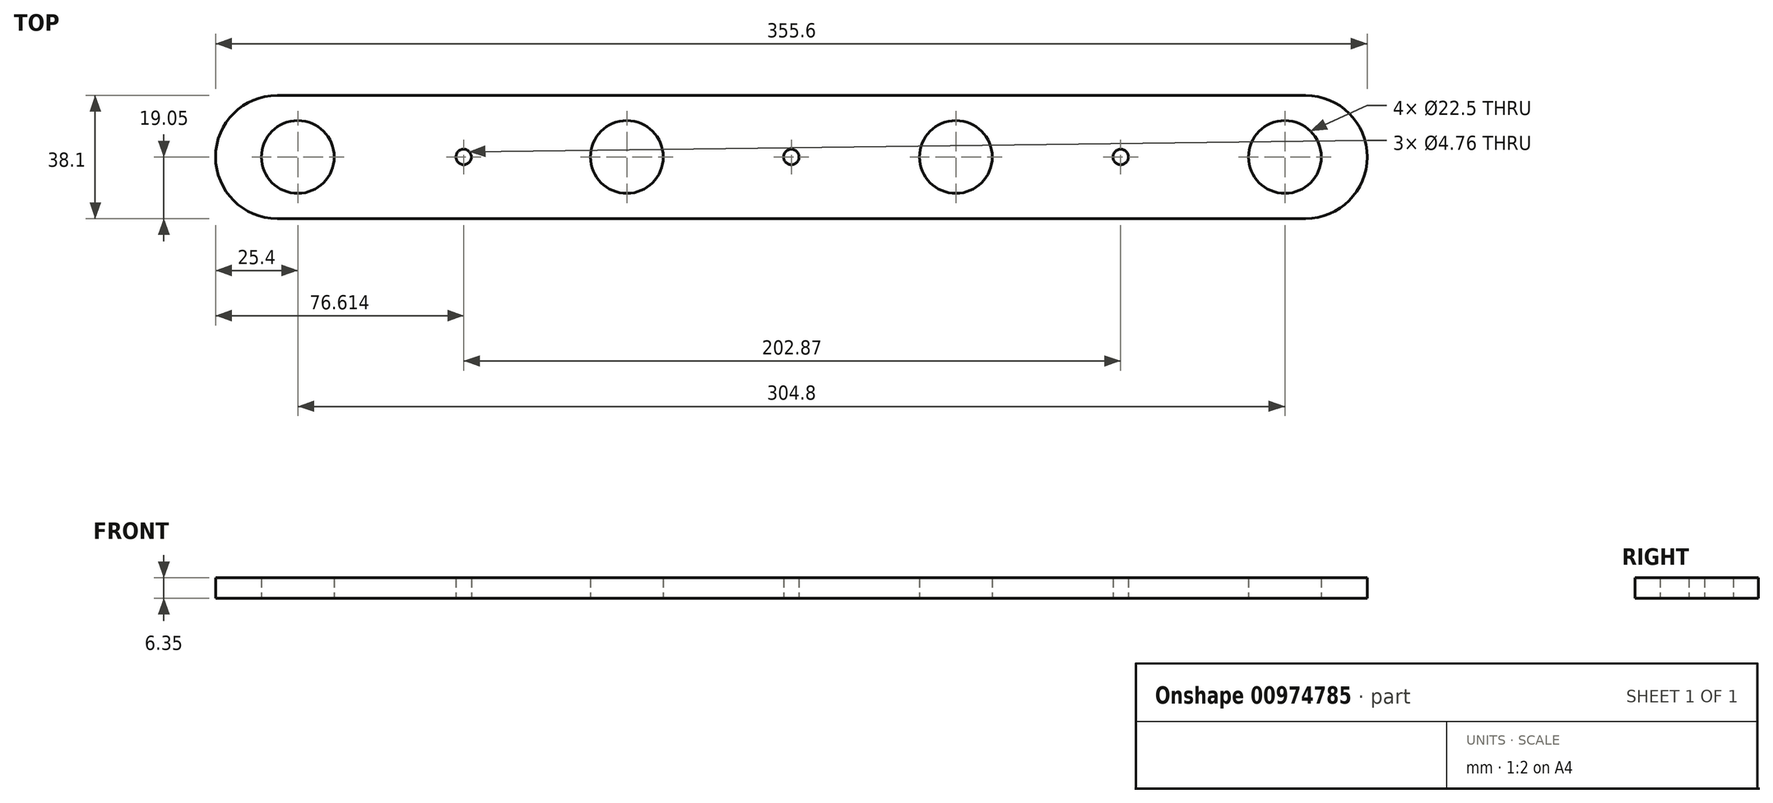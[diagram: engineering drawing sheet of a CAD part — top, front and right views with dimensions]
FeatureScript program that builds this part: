
annotation { "Feature Type Name" : "Feature", "Feature Type Description" : "" }
export const myFeature = defineFeature(function(context is Context, id is Id, definition is map)
    precondition{}
    {
        {
            var Q0;
            Q0=qCreatedBy(makeId("Top.planeOp"),FACE);
            var sketch = newSketch(context, id + "F0", { "sketchPlane" : qUnion([Q0])});
            skLineSegment(sketch, "E0", {"start": v(-158.75, 19.05) * mm, "end": v(158.75, 19.05) * mm});
            skLineSegment(sketch, "E1", {"start": v(-158.75, -19.05) * mm, "end": v(158.75, -19.05) * mm});
            skCircle(sketch, "E2", {"center": v(-50.8, 0) * mm, "radius": 11.25 * mm});
            skCircle(sketch, "E3", {"center": v(50.8, 0) * mm, "radius": 11.25 * mm});
            skPoint(sketch, "E4", {"position": v(0, 0) * mm});
            skPoint(sketch, "E5", {"position": v(-57.15, 0) * mm});
            skCircle(sketch, "E6", {"center": v(152.4, 0) * mm, "radius": 11.25 * mm});
            skPoint(sketch, "E7", {"position": v(158.75, 0) * mm});
            skArc(sketch, "E8", {"start": v(158.75, 19.05) * mm, "mid": v(177.8, 0) * mm, "end": v(158.75, -19.05) * mm});
            skPoint(sketch, "E9", {"position": v(101.6, 0) * mm});
            skCircle(sketch, "E10", {"center": v(-152.4, 0) * mm, "radius": 11.25 * mm});
            skPoint(sketch, "E11", {"position": v(-158.75, 0) * mm});
            skArc(sketch, "E12", {"start": v(-158.75, -19.05) * mm, "mid": v(-177.8, 0) * mm, "end": v(-158.75, 19.05) * mm});
            skPoint(sketch, "E13", {"position": v(-101.6, 0) * mm});
            skSolve(sketch);
        }
        {
            var Q0;
            Q0=qCreatedBy(makeId("Top.planeOp"),FACE);
            var sketch = newSketch(context, id + "F1", { "sketchPlane" : qUnion([Q0])});
            skCircle(sketch, "E14", {"center": v(-101.19, 0) * mm, "radius": 2.38 * mm});
            skCircle(sketch, "E15", {"center": v(0, 0) * mm, "radius": 2.38 * mm});
            skCircle(sketch, "E16", {"center": v(101.68, 0) * mm, "radius": 2.38 * mm});
            skSolve(sketch);
        }
        {
            var Q0;
            Q0 = qSketchRegion(id + "F0", true);
            extrude(context, id + "F2", {"entities" : qUnion([Q0]), "depth" : 6.35 * mm, "offsetDistance" : 25.4 * mm});
        }
        {
            var Q0;
            Q0 = qSketchRegion(id + "F1", true);
            extrude(context, id + "F3", {"entities" : qUnion([Q0]), "operationType" : NewBodyOperationType.REMOVE, "depth" : 25.4 * mm, "offsetDistance" : 25.4 * mm});
        }
    });
